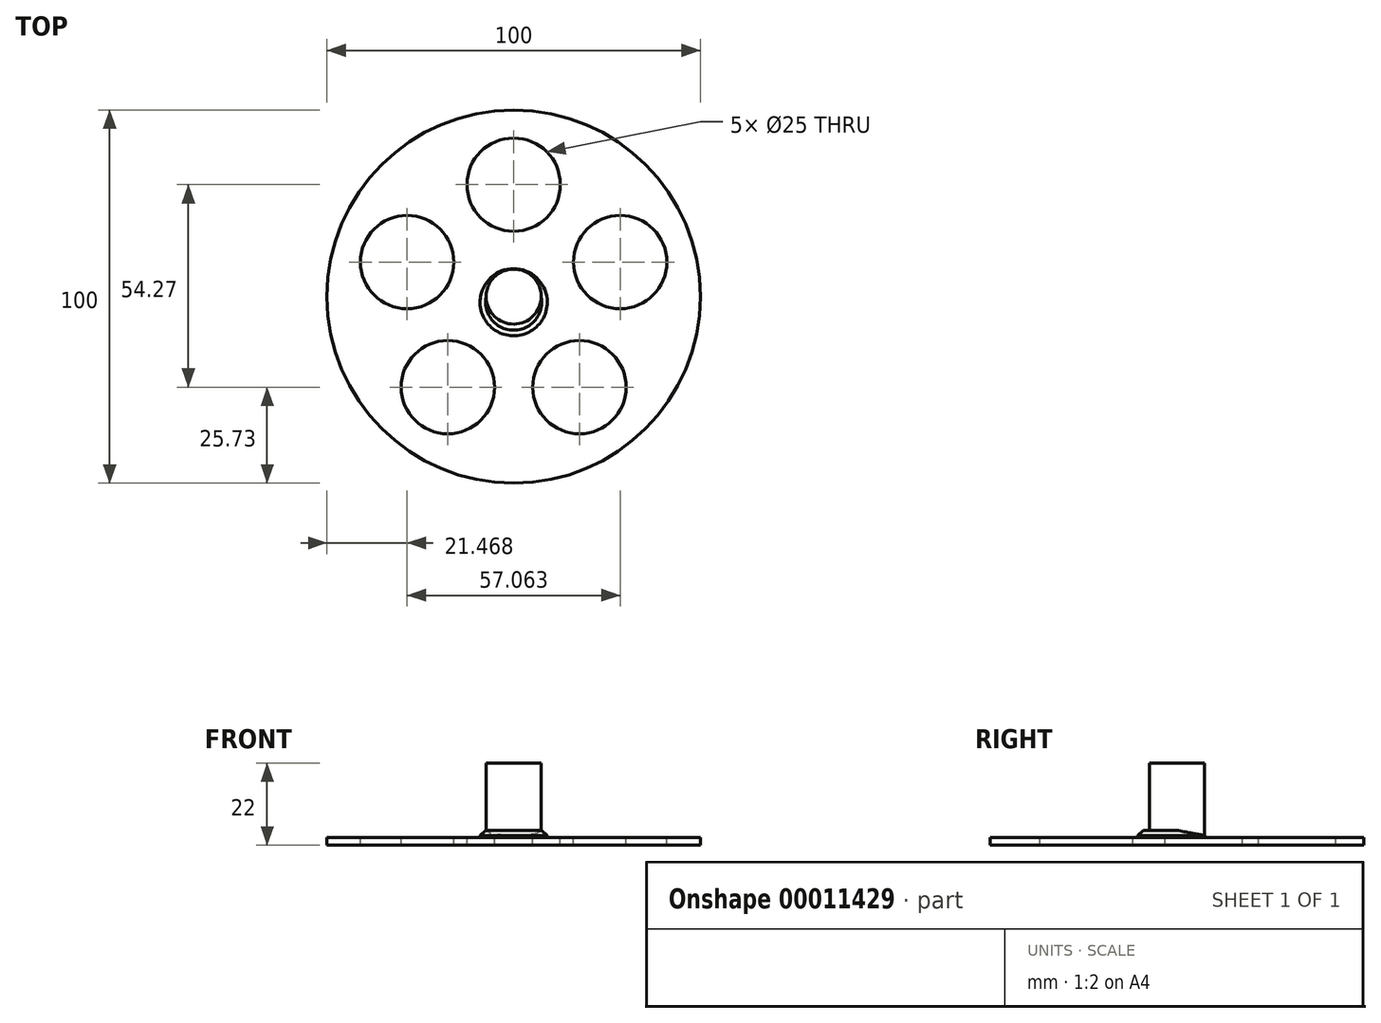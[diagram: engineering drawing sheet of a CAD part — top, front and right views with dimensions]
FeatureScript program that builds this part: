
annotation { "Feature Type Name" : "Feature", "Feature Type Description" : "" }
export const myFeature = defineFeature(function(context is Context, id is Id, definition is map)
    precondition{}
    {
        {
            var Q0;
            Q0=qCreatedBy(makeId("Top.planeOp"),FACE);
            var sketch = newSketch(context, id + "F0", { "sketchPlane" : qUnion([Q0])});
            skCircle(sketch, "E0", {"center": v(0, 0) * mm, "radius": 50 * mm});
            skSolve(sketch);
        }
        {
            var Q0;
            Q0 = qSketchRegion(id + "F0", true);
            extrude(context, id + "F1", {"entities" : qUnion([Q0]), "depth" : 2 * mm});
        }
        {
            var Q0;
            Q0=makeQuery(id+"F1.opExtrude","CAP_FACE",FACE,{"disambiguationData":[OSD([sQuery(id+"F0.wireOp",EDGE,"E0")])],"isStart":false});
            var sketch = newSketch(context, id + "F2", { "sketchPlane" : qUnion([Q0])});
            skCircle(sketch, "E1", {"center": v(0, 0) * mm, "radius": 7.38 * mm});
            skSolve(sketch);
        }
        {
            var Q0;
            Q0 = qSketchRegion(id + "F2", true);
            extrude(context, id + "F3", {"entities" : qUnion([Q0]), "operationType" : NewBodyOperationType.ADD, "depth" : 20 * mm});
        }
        {
            var Q0;
            Q0=makeQuery(id+"F1.opExtrude","CAP_FACE",FACE,{"disambiguationData":[OSD([sQuery(id+"F0.wireOp",EDGE,"E0")])],"isStart":false});
            var sketch = newSketch(context, id + "F4", { "sketchPlane" : qUnion([Q0])});
            skCircle(sketch, "E2", {"center": v(0, 0) * mm, "radius": 30 * mm, "construction": true});
            skCircle(sketch, "E3", {"center": v(0, 30) * mm, "radius": 12.5 * mm});
            skCircle(sketch, "E4.1.0", {"center": v(-28.53, 9.27) * mm, "radius": 12.5 * mm});
            skCircle(sketch, "E4.2.0", {"center": v(-17.63, -24.27) * mm, "radius": 12.5 * mm});
            skCircle(sketch, "E4.3.0", {"center": v(17.63, -24.27) * mm, "radius": 12.5 * mm});
            skCircle(sketch, "E4.4.0", {"center": v(28.53, 9.27) * mm, "radius": 12.5 * mm});
            skSolve(sketch);
        }
        {
            var Q0;
            Q0 = qSketchRegion(id + "F4", true);
            extrude(context, id + "F5", {"entities" : qUnion([Q0]), "operationType" : NewBodyOperationType.REMOVE, "oppositeDirection" : true, "depth" : 25 * mm});
        }
        {
            var Q0;
            Q0=makeQuery(id+"F1.opExtrude","CAP_FACE",FACE,{"disambiguationData":[OSD([sQuery(id+"F0.wireOp",EDGE,"E0")])],"isStart":false});
            var sketch = newSketch(context, id + "F6", { "sketchPlane" : qUnion([Q0])});
            skCircle(sketch, "E5", {"center": v(0, -1.5) * mm, "radius": 9 * mm});
            skSolve(sketch);
        }
        {
            var Q0;
            Q0 = qSketchRegion(id + "F6", true);
            extrude(context, id + "F7", {"entities" : qUnion([Q0]), "operationType" : NewBodyOperationType.ADD, "depth" : 2 * mm});
        }
        {
            var Q0;
            Q0=makeQuery(id+"F7.opExtrude","CAP_EDGE",EDGE,{"disambiguationData":[OSD([sQuery(id+"F6.wireOp",EDGE,"E5")])],"isStart":false});
            chamfer(context, id + "F8", {"entities" : qUnion([Q0]), "width" : 1.5 * mm, "tangentPropagation" : true});
        }
    });
